# Revit family: MP_Одностворчатая правая (Душевые)
name_source: partatom
category: Двери
units: mm (PartAtom-declared; Revit-internal decimal feet)

## family parameters
Всегда вертикально = Да
Общий = Нет
Основа = Стена
При загрузке вырезать с полостями = Нет
Точка принадлежности помещению = Нет

## types (6) — shared parameters
MP_Кол-во створок/открывание = 1 Пр
not_Ручка штанга = Да
Аналитическая конструкция = <Нет>
Группа модели = Дверь в стене
Единица измерения = шт.
Зазор. Сверху = 2 мм
Зазор. Слева = 2 мм
Зазор. Справа = 2 мм
Замыкание стены = По основе
Наименование = Однопольная.Глухая.Распашная
Однопольная.Глухая = Однопольная.Глухая.Распашная
Однопольная.Остеклённая = Однопольная.Остеклённая.Распашная
Описание = Двери
Определить тепловые свойства по = Тип схем
Открытие.Внутрь = Нет
Открытие.Наружу = Да
Полотно.Рама.Ширина вверху = 50 мм
Полотно.Рама.Ширина внизу = 50 мм
Полотно.Рама.Ширина слева = 50 мм
Полотно.Рама.Ширина справа = 50 мм
Порог = Нет
Ручка_Круглая_Штанга_План = Нет
Ручка_Нажимная_Высота = 1000 мм
Ручка_Штанга = Нет
Ручка_Штанга_Высота = 1400 мм
Ручка_Штанга_План = Нет
Стекло.Толщина = 20 мм
Тип конструкций = Дверь
Тип ручки штанги_Круглая = АС-Ручка двери : АС-Штанга-Круглая
Толщина = 40 мм
Угол открывания = 90.00°
Функция = Внутренние слои
zero-valued in all types: MP_Масса_кг, Порог. Смещение

## per-type parameters (varying)
- Д-12пр_1600х740_Г_(700 в свету)_в душевые: MP_Высота в свету=1578 мм; MP_Высота полотна=1578 мм; MP_Констркуция коробки=Дверная алюминиевая коробка скрытой установки NAYADA-Stels; MP_Описание=Дверной блок внутренний, однопольный, распашной, глухой, правого откравыния по типу NAYADA-Stels. Толщина 60 мм.; MP_Площадь=1.18 м²; MP_Тип полотна=. : Глухое; MP_Ширина=740 мм; MP_Ширина в свету=656 мм; MP_Ширина полотна=696 мм; Высота=1600 мм; Коробка. Глубина=20 мм; Коробка. Толщина=20 мм; Материал коробки=Металлические двери_RAL 9002; Материал остекления=<По категории>; Материал полотна=Металлические двери_RAL 9002; Материал фурнитуры=<По категории>; Метериал уплотнителя=Металлические двери_RAL 9002; Огнестойкость=-; Полотно. Толщина=20 мм; Примерная высота=1598 мм; Примерная ширина=736 мм; Ручка_Нажимная=Нет; Ручка_Нажимная_Накладка для замка=Нет; Ручка_Штанга_Высота до верха=1800 мм; Тип ручки штанги=АС-Ручка двери : АС-Штанга; Ширина=740 мм; Ширина проема=740 мм
- Д-11п_2100х1100_Г_EIS 60_(1000 в свету)_ЛК: MP_Высота в свету=2050 мм; MP_Высота полотна=2050 мм; MP_Констркуция коробки=Телескопический добор, алюминий; MP_Обозначение=ГОСТ 23747-2015; MP_Описание=Дверной блок внутренний, противопожарный, однопольный, распашной, глухой, левого откравыния по типу NAYADA. Толщина  мм.; MP_Площадь=2.31 м²; MP_Тип полотна=. : Остекленное; MP_Ширина=1100 мм; MP_Ширина активного полотна=940; MP_Ширина в свету=960 мм; MP_Ширина полотна=1000 мм; Высота=2100 мм; Код оборудования=ДАВ О Оп Пр  П  Р; Комментарии к типоразмеру=Двери в ЛК, тамбур-шлюз; Коробка. Глубина=250 мм; Коробка. Толщина=48 мм; Марка=ДВ-2.2пр; Материал коробки=Металлические двери_134-GG (ZDT-004); Материал остекления=Стело_Двери; Материал полотна=Металлические двери_134-GG (ZDT-004); Материал фурнитуры=Металлические двери_134-GG (ZDT-004); Метериал уплотнителя=Металлические двери_134-GG (ZDT-004); Огнестойкость=EIS 60; Полотно. Толщина=60 мм; Примерная высота=2098 мм; Примерная ширина=1096 мм; Ручка_Нажимная=Да; Ручка_Нажимная_Накладка для замка=Нет; Ручка_Штанга_Высота до верха=1700 мм; Тип ручки штанги=АС-Ручка двери : АС-Штанга-Круглая; Ширина=1100 мм; Ширина проема=1100 мм; короткое наименование=ДПС 01 2500х1200 п EI 30
- Д-2.4п_2150х1100_Г_EI 30_(1000 в свету)_в раздевальную: MP_Высота в свету=2100 мм; MP_Высота полотна=2100 мм; MP_Констркуция коробки=Дверная алюминиевая коробка скрытой установки NAYADA; MP_Обозначение=ГОСТ 23747-2015; MP_Описание=Дверной блок внутренний, противопожарный, однопольный, распашной, глухой, правого откравыния по типу NAYADA. Толщина 60 мм.; MP_Площадь=2.37 м²; MP_Тип полотна=. : Остекленное; MP_Ширина=1100 мм; MP_Ширина активного полотна=940; MP_Ширина в свету=960 мм; MP_Ширина полотна=1000 мм; Высота=2150 мм; Код оборудования=ДАВ О Оп Пр  П  Р; Комментарии к типоразмеру=Двери в ЛК, тамбур-шлюз; Коробка. Глубина=250 мм; Коробка. Толщина=48 мм; Марка=ДВ-2.2пр; Материал коробки=Металлические двери_134-GG (ZDT-004); Материал остекления=Стело_Двери; Материал полотна=Металлические двери_134-GG (ZDT-004); Материал фурнитуры=Металлические двери_134-GG (ZDT-004); Метериал уплотнителя=Металлические двери_134-GG (ZDT-004); Огнестойкость=EI 30; Полотно. Толщина=60 мм; Примерная высота=2148 мм; Примерная ширина=1096 мм; Ручка_Нажимная=Да; Ручка_Нажимная_Накладка для замка=Нет; Ручка_Штанга_Высота до верха=1700 мм; Тип ручки штанги=АС-Ручка двери : АС-Штанга-Круглая; Ширина=1100 мм; Ширина проема=1100 мм; короткое наименование=ДПС 01 2500х1200 п EI 30
- Д-5.1пр_2150х800_Г_(700 в свету)_дверь в санузел: MP_Высота в свету=2106 мм; MP_Высота полотна=2106 мм; MP_Констркуция коробки=Дверная алюминиевая коробка скрытой установки NAYADA-Stels; MP_Описание=Дверной блок внутренний, однопольный, распашной, глухой, правого откравыния по типу NAYADA-Stels. Толщина 60 мм.; MP_Площадь=1.72 м²; MP_Тип полотна=. : Глухое; MP_Ширина=800 мм; MP_Ширина в свету=671 мм; MP_Ширина полотна=711 мм; Высота=2150 мм; Коробка. Глубина=118 мм; Коробка. Толщина=43 мм; Материал коробки=Металлические двери_RAL 9002; Материал остекления=<По категории>; Материал полотна=Металлические двери_RAL 9002; Материал фурнитуры=<По категории>; Метериал уплотнителя=Металлические двери_RAL 9002; Огнестойкость=-; Полотно. Толщина=60 мм; Примерная высота=2148 мм; Примерная ширина=796 мм; Ручка_Нажимная=Да; Ручка_Нажимная_Накладка для замка=Да; Ручка_Штанга_Высота до верха=1800 мм; Тип ручки штанги=АС-Ручка двери : АС-Штанга; Ширина=800 мм; Ширина проема=800 мм
- Д-2.2п_2150х1100_Г_EI 30_(1000 в свету)_в комнату ребенка и родителей: MP_Высота в свету=2100 мм; MP_Высота полотна=2100 мм; MP_Констркуция коробки=Дверная алюминиевая коробка скрытой установки NAYADA; MP_Обозначение=ГОСТ 23747-2015; MP_Описание=Дверной блок внутренний, противопожарный, однопольный, распашной, глухой, правого откравыния по типу NAYADA. Толщина 60 мм.; MP_Площадь=2.37 м²; MP_Тип полотна=. : Остекленное; MP_Ширина=1100 мм; MP_Ширина активного полотна=940; MP_Ширина в свету=960 мм; MP_Ширина полотна=1000 мм; Высота=2150 мм; Код оборудования=ДАВ О Оп Пр  П  Р; Комментарии к типоразмеру=Двери в ЛК, тамбур-шлюз; Коробка. Глубина=124 мм; Коробка. Толщина=48 мм; Марка=ДВ-2.2пр; Материал коробки=Металлические двери_134-GG (ZDT-004); Материал остекления=Стело_Двери; Материал полотна=Металлические двери_134-GG (ZDT-004); Материал фурнитуры=Металлические двери_134-GG (ZDT-004); Метериал уплотнителя=Металлические двери_134-GG (ZDT-004); Огнестойкость=EI 30; Полотно. Толщина=60 мм; Примерная высота=2148 мм; Примерная ширина=1096 мм; Ручка_Нажимная=Да; Ручка_Нажимная_Накладка для замка=Нет; Ручка_Штанга_Высота до верха=1700 мм; Тип ручки штанги=АС-Ручка двери : АС-Штанга-Круглая; Ширина=1100 мм; Ширина проема=1100 мм; короткое наименование=ДПС 01 2500х1200 п EI 30
- Д-5.3пр_2150х800_Г_(700 в свету)_в санузел: MP_Высота в свету=2106 мм; MP_Высота полотна=2106 мм; MP_Констркуция коробки=Дверная алюминиевая коробка скрытой установки NAYADA-Stels; MP_Описание=Дверной блок внутренний, однопольный, распашной, глухой, правого откравыния по типу NAYADA-Stels. Толщина 60 мм.; MP_Площадь=1.72 м²; MP_Тип полотна=. : Глухое; MP_Ширина=800 мм; MP_Ширина в свету=671 мм; MP_Ширина полотна=711 мм; Высота=2150 мм; Коробка. Глубина=118 мм; Коробка. Толщина=43 мм; Материал коробки=Металлические двери_RAL 9002; Материал остекления=<По категории>; Материал полотна=Металлические двери_RAL 9002; Материал фурнитуры=<По категории>; Метериал уплотнителя=Металлические двери_RAL 9002; Огнестойкость=-; Полотно. Толщина=60 мм; Примерная высота=2148 мм; Примерная ширина=796 мм; Ручка_Нажимная=Да; Ручка_Нажимная_Накладка для замка=Да; Ручка_Штанга_Высота до верха=1800 мм; Тип ручки штанги=АС-Ручка двери : АС-Штанга; Ширина=800 мм; Ширина проема=800 мм

## geometry (parser evidence)
native form markers: Sweep x3
no freeform markers — native parametric forms only
